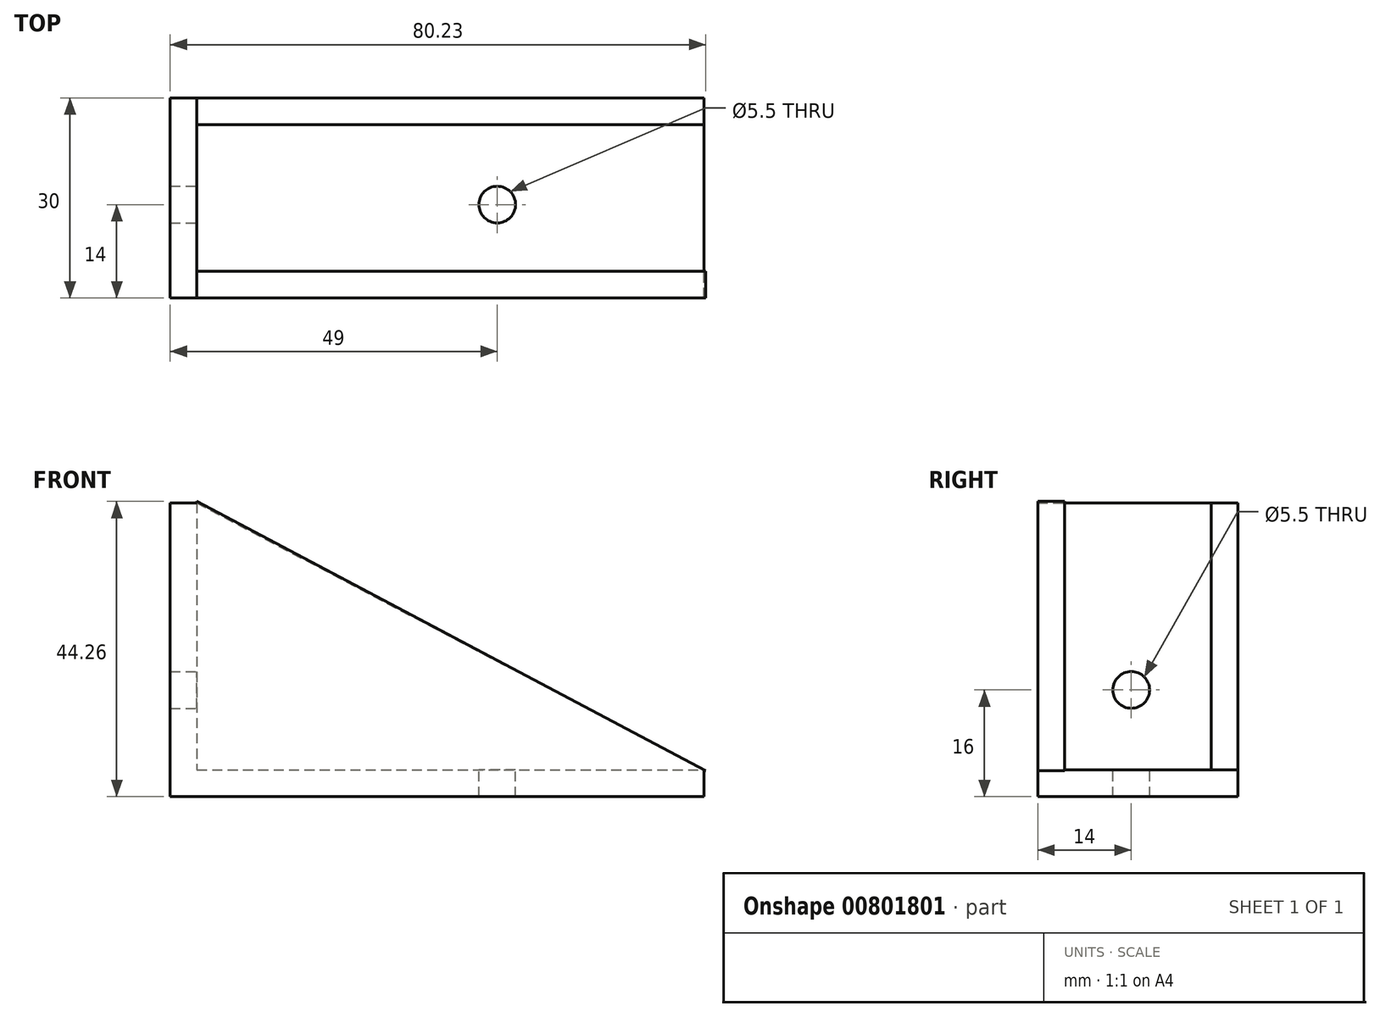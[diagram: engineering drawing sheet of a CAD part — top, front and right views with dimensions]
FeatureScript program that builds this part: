
annotation { "Feature Type Name" : "Feature", "Feature Type Description" : "" }
export const myFeature = defineFeature(function(context is Context, id is Id, definition is map)
    precondition{}
    {
        {
            var Q0;
            Q0=qCreatedBy(makeId("Top.planeOp"),FACE);
            var sketch = newSketch(context, id + "F0", { "sketchPlane" : qUnion([Q0])});
            skLineSegment(sketch, "E0.bottom", {"start": v(0, 0) * mm, "end": v(80, 0) * mm});
            skLineSegment(sketch, "E0.top", {"start": v(0, 30) * mm, "end": v(80, 30) * mm});
            skLineSegment(sketch, "E0.left", {"start": v(0, 0) * mm, "end": v(0, 30) * mm});
            skLineSegment(sketch, "E0.right", {"start": v(80, 0) * mm, "end": v(80, 30) * mm});
            skSolve(sketch);
        }
        {
            var Q0;
            Q0=makeQuery(id+"F0.imprint","IMPRINT",FACE,{"disambiguationData":[TD([[makeQuery(id+"F0.imprint","IMPRINT",EDGE,{"derivedFrom":sQuery(id+"F0.wireOp",EDGE,"E0.bottom")}),1.0]])]});
            extrude(context, id + "F1", {"entities" : qUnion([Q0]), "depth" : 4 * mm});
        }
        {
            var Q0;
            Q0=makeQuery(id+"F1.opExtrude","CAP_FACE",FACE,{"disambiguationData":[OSD([sQuery(id+"F0.wireOp",EDGE,"E0.bottom"),sQuery(id+"F0.wireOp",EDGE,"E0.top"),sQuery(id+"F0.wireOp",EDGE,"E0.left"),sQuery(id+"F0.wireOp",EDGE,"E0.right")])],"isStart":false});
            var sketch = newSketch(context, id + "F2", { "sketchPlane" : qUnion([Q0])});
            skLineSegment(sketch, "E1.bottom", {"start": v(0, 0) * mm, "end": v(4, 0) * mm});
            skLineSegment(sketch, "E1.top", {"start": v(0, 30) * mm, "end": v(4, 30) * mm});
            skLineSegment(sketch, "E1.left", {"start": v(0, 0) * mm, "end": v(0, 30) * mm});
            skLineSegment(sketch, "E1.right", {"start": v(4, 0) * mm, "end": v(4, 30) * mm});
            skSolve(sketch);
        }
        {
            var Q0;
            Q0=makeQuery(id+"F2.imprint","IMPRINT",FACE,{"disambiguationData":[TD([[makeQuery(id+"F2.imprint","IMPRINT",EDGE,{"derivedFrom":sQuery(id+"F2.wireOp",EDGE,"E1.bottom")}),1.0]])]});
            extrude(context, id + "F3", {"entities" : qUnion([Q0]), "operationType" : NewBodyOperationType.ADD, "depth" : 40 * mm});
        }
        {
            var Q0;
            Q0=qCreatedBy(makeId("Front.planeOp"),FACE);
            var sketch = newSketch(context, id + "F4", { "sketchPlane" : qUnion([Q0])});
            skLineSegment(sketch, "E2", {"start": v(4, 44.26) * mm, "end": v(80.23, 3.91) * mm});
            skLineSegment(sketch, "E3", {"start": v(80.23, 3.91) * mm, "end": v(2.15, 3.91) * mm});
            skLineSegment(sketch, "E4", {"start": v(2.15, 3.91) * mm, "end": v(4, 44.26) * mm});
            skSolve(sketch);
        }
        {
            var Q0;
            Q0=makeQuery(id+"F4.imprint","IMPRINT",FACE,{"disambiguationData":[TD([[makeQuery(id+"F4.imprint","IMPRINT",EDGE,{"derivedFrom":sQuery(id+"F4.wireOp",EDGE,"E2")}),-1.0]])]});
            extrude(context, id + "F5", {"entities" : qUnion([Q0]), "operationType" : NewBodyOperationType.ADD, "oppositeDirection" : true, "depth" : 4 * mm});
        }
        {
            var Q0;
            Q0=makeQuery(id+"F3.boolean.opBoolean","MERGE",FACE,{"derivedFrom":[makeQuery(id+"F1.opExtrude","SWEPT_FACE",FACE,{"disambiguationData":[OSD([sQuery(id+"F0.wireOp",EDGE,"E0.top")])]}),makeQuery(id+"F3.opExtrude","SWEPT_FACE",FACE,{"disambiguationData":[OSD([sQuery(id+"F2.wireOp",EDGE,"E1.top")])]})]});
            var sketch = newSketch(context, id + "F6", { "sketchPlane" : qUnion([Q0])});
            skLineSegment(sketch, "E5", {"start": v(-4, 44) * mm, "end": v(-80, 4) * mm});
            skLineSegment(sketch, "E6", {"start": v(-80, 4) * mm, "end": v(-2.73, 1.96) * mm});
            skLineSegment(sketch, "E7", {"start": v(-2.73, 1.96) * mm, "end": v(-4, 44) * mm});
            skSolve(sketch);
        }
        {
            var Q0;
            Q0=makeQuery(id+"F6.imprint","IMPRINT",FACE,{"disambiguationData":[TD([[makeQuery(id+"F6.imprint","IMPRINT",EDGE,{"derivedFrom":sQuery(id+"F6.wireOp",EDGE,"E5")}),1.0]])]});
            var Q1;
            Q1=makeQuery(id+"F6.imprint","IMPRINT",FACE,{"disambiguationData":[TD([[makeQuery(id+"F6.imprint","IMPRINT",EDGE,{"derivedFrom":sQuery(id+"F6.wireOp",EDGE,"E6")}),-1.0]])]});
            extrude(context, id + "F7", {"entities" : qUnion([Q0, Q1]), "operationType" : NewBodyOperationType.ADD, "oppositeDirection" : true, "depth" : 4 * mm});
        }
        {
            var Q0;
            Q0=makeQuery(id+"F1.opExtrude","CAP_FACE",FACE,{"disambiguationData":[OSD([sQuery(id+"F0.wireOp",EDGE,"E0.bottom"),sQuery(id+"F0.wireOp",EDGE,"E0.top"),sQuery(id+"F0.wireOp",EDGE,"E0.left"),sQuery(id+"F0.wireOp",EDGE,"E0.right")])],"isStart":false});
            var sketch = newSketch(context, id + "F8", { "sketchPlane" : qUnion([Q0])});
            skCircle(sketch, "E8", {"center": v(49, 14) * mm, "radius": 2.75 * mm});
            skSolve(sketch);
        }
        {
            var Q0;
            Q0=makeQuery(id+"F8.imprint","IMPRINT",FACE,{"disambiguationData":[TD([[makeQuery(id+"F8.imprint","IMPRINT",EDGE,{"derivedFrom":sQuery(id+"F8.wireOp",EDGE,"E8")}),1.0]])]});
            extrude(context, id + "F9", {"entities" : qUnion([Q0]), "operationType" : NewBodyOperationType.REMOVE, "oppositeDirection" : true, "depth" : 25 * mm});
        }
        {
            var Q0;
            Q0=makeQuery(id+"F3.opExtrude","SWEPT_FACE",FACE,{"disambiguationData":[OSD([sQuery(id+"F2.wireOp",EDGE,"E1.right")])]});
            var sketch = newSketch(context, id + "F10", { "sketchPlane" : qUnion([Q0])});
            skCircle(sketch, "E9", {"center": v(14, 16) * mm, "radius": 2.75 * mm});
            skCircle(sketch, "E10", {"center": v(13.57, 35.32) * mm, "radius": 3.42 * mm});
            skSolve(sketch);
        }
        {
            var Q0;
            Q0=makeQuery(id+"F10.imprint","IMPRINT",FACE,{"disambiguationData":[TD([[makeQuery(id+"F10.imprint","IMPRINT",EDGE,{"derivedFrom":sQuery(id+"F10.wireOp",EDGE,"E9")}),1.0]])]});
            extrude(context, id + "F11", {"entities" : qUnion([Q0]), "operationType" : NewBodyOperationType.REMOVE, "oppositeDirection" : true, "depth" : 25 * mm});
        }
    });
